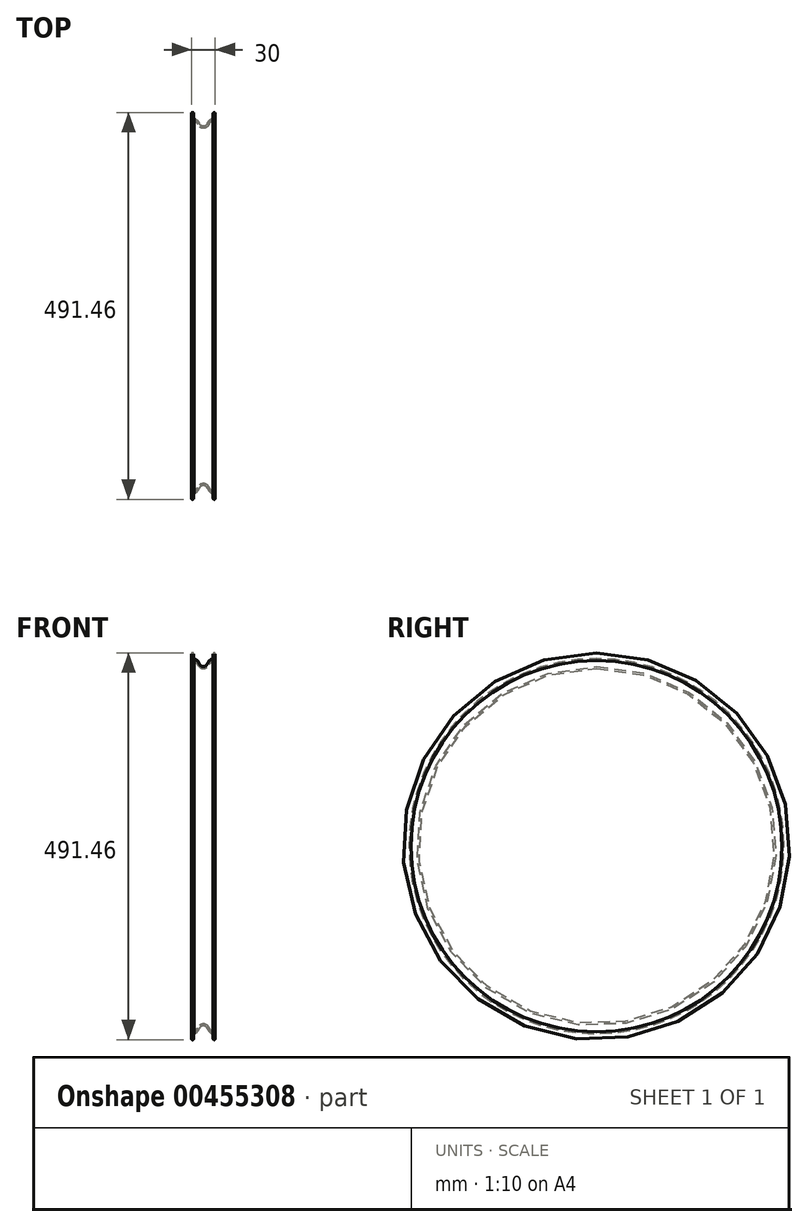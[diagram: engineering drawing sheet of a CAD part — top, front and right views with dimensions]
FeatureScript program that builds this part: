
annotation { "Feature Type Name" : "Feature", "Feature Type Description" : "" }
export const myFeature = defineFeature(function(context is Context, id is Id, definition is map)
    precondition{}
    {
        {
            var Q0;
            Q0=qCreatedBy(makeId("Front.planeOp"),FACE);
            var sketch = newSketch(context, id + "F0", { "sketchPlane" : qUnion([Q0])});
            skLineSegment(sketch, "E0", {"start": v(0, 285) * mm, "end": v(0, 0) * mm, "construction": true});
            skArc(sketch, "E1", {"start": v(15.32, 246.02) * mm, "mid": v(0, 285) * mm, "end": v(-15.32, 246.02) * mm, "construction": true});
            skArc(sketch, "E2", {"start": v(-15, 238.73) * mm, "mid": v(-14.32, 236.82) * mm, "end": v(-12.57, 235.78) * mm});
            skArc(sketch, "E3", {"start": v(-7.5, 230.95) * mm, "mid": v(-9.48, 233.95) * mm, "end": v(-12.57, 235.78) * mm});
            skArc(sketch, "E4", {"start": v(-7.5, 230.95) * mm, "mid": v(-4.57, 227.16) * mm, "end": v(0, 225.73) * mm});
            skArc(sketch, "E5.0", {"start": v(-5.16, 231.82) * mm, "mid": v(-3.14, 229.21) * mm, "end": v(0, 228.23) * mm});
            skArc(sketch, "E6.0", {"start": v(-5.16, 231.82) * mm, "mid": v(-7.83, 235.83) * mm, "end": v(-12.02, 238.23) * mm});
            skLineSegment(sketch, "E7", {"start": v(-12.5, 244.48) * mm, "end": v(-12.5, 238.73) * mm});
            skArc(sketch, "E8", {"start": v(-12.5, 238.73) * mm, "mid": v(-12.36, 238.38) * mm, "end": v(-12.02, 238.23) * mm});
            skArc(sketch, "E9.MirrorCS", {"start": v(12.5, 238.73) * mm, "mid": v(12.36, 238.38) * mm, "end": v(12.02, 238.23) * mm});
            skLineSegment(sketch, "E10.MirrorCS", {"start": v(12.5, 244.48) * mm, "end": v(12.5, 238.73) * mm});
            skArc(sketch, "E11.MirrorCS", {"start": v(5.16, 231.82) * mm, "mid": v(7.83, 235.83) * mm, "end": v(12.02, 238.23) * mm});
            skArc(sketch, "E12.MirrorCS", {"start": v(7.5, 230.95) * mm, "mid": v(9.48, 233.95) * mm, "end": v(12.57, 235.78) * mm});
            skArc(sketch, "E13.MirrorCS", {"start": v(5.16, 231.82) * mm, "mid": v(3.14, 229.21) * mm, "end": v(0, 228.23) * mm});
            skArc(sketch, "E14.MirrorCS", {"start": v(15, 238.73) * mm, "mid": v(14.32, 236.82) * mm, "end": v(12.57, 235.78) * mm});
            skArc(sketch, "E15.MirrorCS", {"start": v(7.5, 230.95) * mm, "mid": v(4.57, 227.16) * mm, "end": v(0, 225.73) * mm});
            skLineSegment(sketch, "E16.MirrorCS", {"start": v(15, 244.48) * mm, "end": v(15, 238.73) * mm});
            skArc(sketch, "E17", {"start": v(-12.5, 244.48) * mm, "mid": v(-13.75, 245.73) * mm, "end": v(-15, 244.48) * mm});
            skPoint(sketch, "E18.orphan", {"position": v(-15, 245.73) * mm});
            skPoint(sketch, "E19.orphan", {"position": v(-12.5, 245.73) * mm});
            skLineSegment(sketch, "E20", {"start": v(-15, 238.73) * mm, "end": v(-15, 244.48) * mm});
            skPoint(sketch, "E21.orphan", {"position": v(-13.75, 243.23) * mm});
            skPoint(sketch, "E22.orphan", {"position": v(-13.75, 245.73) * mm});
            skArc(sketch, "E23.MirrorCS", {"start": v(12.5, 244.48) * mm, "mid": v(13.75, 245.73) * mm, "end": v(15, 244.48) * mm});
            skPoint(sketch, "E24.orphan", {"position": v(15, 245.73) * mm});
            skPoint(sketch, "E25.orphan", {"position": v(12.5, 245.73) * mm});
            skArc(sketch, "E26", {"start": v(-12.5, 244.48) * mm, "mid": v(-13.18, 245.7) * mm, "end": v(-14.57, 245.86) * mm, "construction": true});
            skArc(sketch, "E27", {"start": v(-15.32, 246.02) * mm, "mid": v(-14.96, 245.87) * mm, "end": v(-14.57, 245.86) * mm, "construction": true});
            skArc(sketch, "E28.MirrorCS", {"start": v(12.5, 244.48) * mm, "mid": v(13.18, 245.7) * mm, "end": v(14.57, 245.86) * mm, "construction": true});
            skArc(sketch, "E29.MirrorCS", {"start": v(15.32, 246.02) * mm, "mid": v(14.96, 245.87) * mm, "end": v(14.57, 245.86) * mm, "construction": true});
            skSolve(sketch);
        }
        {
            var Q0;
            Q0=qCreatedBy(makeId("Right.planeOp"),FACE);
            var sketch = newSketch(context, id + "F1", { "sketchPlane" : qUnion([Q0])});
            skCircle(sketch, "E30", {"center": v(0, 0) * mm, "radius": 262.5 * mm, "construction": true});
            skSolve(sketch);
        }
        {
            var Q0;
            Q0=makeQuery(id+"F0.imprint","IMPRINT",FACE,{"disambiguationData":[TD([[makeQuery(id+"F0.imprint","IMPRINT",EDGE,{"derivedFrom":sQuery(id+"F0.wireOp",EDGE,"E2")}),1.0]])]});
            var Q1;
            Q1=sQuery(id+"F1.wireOp",EDGE,"E30");
            revolve(context, id + "F2", {"entities" : qUnion([Q0]), "axis" : qUnion([Q1]), "revolveType" : RevolveType.FULL});
        }
        {
            var Q0;
            Q0=qCreatedBy(makeId("Front.planeOp"),FACE);
            var sketch = newSketch(context, id + "F3", { "sketchPlane" : qUnion([Q0])});
            skArc(sketch, "E31.0", {"start": v(-7.5, 230.95) * mm, "mid": v(-4.57, 227.16) * mm, "end": v(0, 225.73) * mm});
            skLineSegment(sketch, "E32", {"start": v(-40, 0) * mm, "end": v(40, 0) * mm, "construction": true});
            skLineSegment(sketch, "E33.MirrorCS", {"start": v(-23, 25) * mm, "end": v(0, 25) * mm});
            skLineSegment(sketch, "E34.MirrorCS", {"start": v(-33.5, 40) * mm, "end": v(-23, 25) * mm});
            skLineSegment(sketch, "E35.MirrorCS", {"start": v(-40, 15) * mm, "end": v(-40, 40) * mm});
            skLineSegment(sketch, "E36.MirrorCS", {"start": v(-40.04, 40) * mm, "end": v(-33.5, 40) * mm});
            skLineSegment(sketch, "E37", {"start": v(0, 15) * mm, "end": v(-40, 15) * mm});
            skPoint(sketch, "E38.orphan", {"position": v(-40, 0) * mm});
            skLineSegment(sketch, "E39.MirrorCS", {"start": v(-33.5, 40) * mm, "end": v(-6.5, 201.63) * mm});
            skLineSegment(sketch, "E40.MirrorCS", {"start": v(-39.43, 39.9) * mm, "end": v(-7.5, 230.95) * mm});
            skPoint(sketch, "E41.visualSharp", {"position": v(-5.77, 205.93) * mm});
            skArc(sketch, "E41.filletArc", {"start": v(-1.06, 205.78) * mm, "mid": v(-4.6, 204.77) * mm, "end": v(-6.5, 201.63) * mm});
            skPoint(sketch, "E42.visualSharp", {"position": v(5.77, 205.93) * mm});
            skLineSegment(sketch, "E43", {"start": v(0, 205.78) * mm, "end": v(-1.06, 205.78) * mm});
            skLineSegment(sketch, "E44", {"start": v(0, 225.73) * mm, "end": v(0, 205.78) * mm});
            skLineSegment(sketch, "E45", {"start": v(0, 15) * mm, "end": v(0, 25) * mm});
            skPoint(sketch, "E46.orphan", {"position": v(40, 15) * mm});
            skPoint(sketch, "E47.orphan", {"position": v(1.06, 205.78) * mm});
            skPoint(sketch, "E48.0.start.orphan", {"position": v(7.5, 230.95) * mm});
            skSolve(sketch);
        }
        {
            var Q0;
            Q0=qCreatedBy(makeId("Front.planeOp"),FACE);
            cPlane(context, id + "F4", {"entities" : qUnion([Q0]), "cplaneType" : CPlaneType.OFFSET, "offset" : 0 * mm, "width" : 150 * mm, "height" : 150 * mm});
        }
    });
